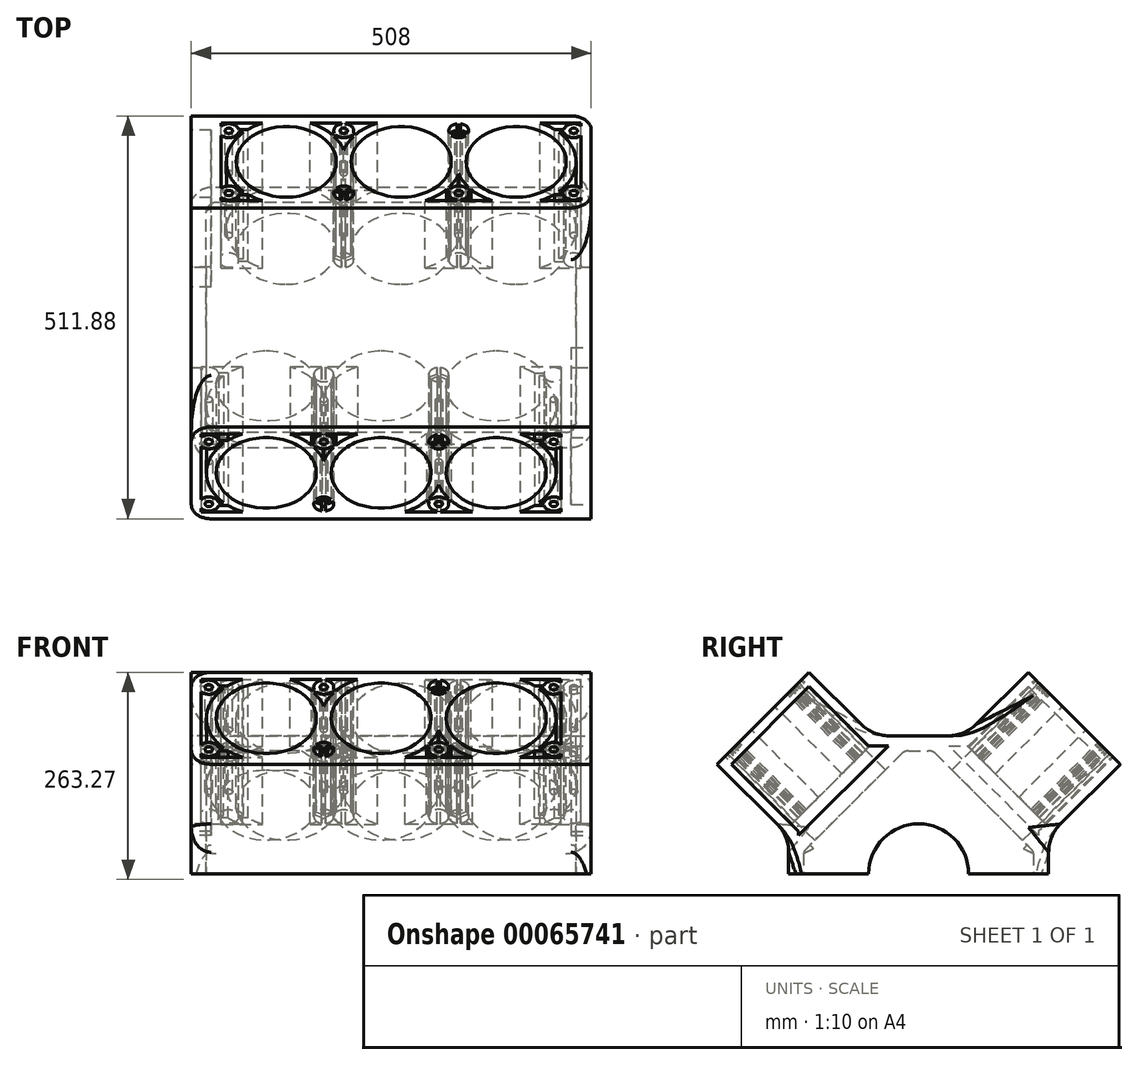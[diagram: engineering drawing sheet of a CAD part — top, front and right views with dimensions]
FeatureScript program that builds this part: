
annotation { "Feature Type Name" : "Feature", "Feature Type Description" : "" }
export const myFeature = defineFeature(function(context is Context, id is Id, definition is map)
    precondition{}
    {
        {
            var Q0;
            Q0=qCreatedBy(makeId("Right.planeOp"),FACE);
            var sketch = newSketch(context, id + "F0", { "sketchPlane" : qUnion([Q0])});
            skLineSegment(sketch, "E0", {"start": v(0, 175.36) * mm, "end": v(0, 0) * mm, "construction": true});
            skLineSegment(sketch, "E1", {"start": v(0, 0) * mm, "end": v(197.57, 197.57) * mm, "construction": true});
            skLineSegment(sketch, "E2", {"start": v(0, 175.36) * mm, "end": v(58.61, 175.36) * mm});
            skLineSegment(sketch, "E3", {"start": v(58.61, 175.36) * mm, "end": v(139.2, 255.94) * mm});
            skLineSegment(sketch, "E4", {"start": v(139.2, 255.94) * mm, "end": v(255.94, 139.2) * mm});
            skLineSegment(sketch, "E5", {"start": v(255.94, 139.2) * mm, "end": v(165.1, 48.36) * mm});
            skLineSegment(sketch, "E6", {"start": v(165.1, 48.36) * mm, "end": v(165.1, 0) * mm});
            skLineSegment(sketch, "E7", {"start": v(63.5, 0) * mm, "end": v(165.1, 0) * mm});
            skArc(sketch, "E8", {"start": v(0, 63.5) * mm, "mid": v(44.9, 44.9) * mm, "end": v(63.5, 0) * mm});
            skLineSegment(sketch, "E9", {"start": v(0, 175.36) * mm, "end": v(0, 63.5) * mm});
            skSolve(sketch);
        }
        {
            var Q0;
            Q0 = qSketchRegion(id + "F0", true);
            extrude(context, id + "F1", {"entities" : qUnion([Q0]), "endBound" : BoundingType.SYMMETRIC, "depth" : 482.6 * mm});
        }
        {
            var Q0;
            Q0=makeQuery(id+"F1.opExtrude","SWEPT_FACE",FACE,{"disambiguationData":[OSD([sQuery(id+"F0.wireOp",EDGE,"E4")])]});
            var sketch = newSketch(context, id + "F2", { "sketchPlane" : qUnion([Q0])});
            skLineSegment(sketch, "E10", {"start": v(146.05, 0) * mm, "end": v(-146.05, 0) * mm, "construction": true});
            skCircle(sketch, "E11", {"center": v(146.05, 0) * mm, "radius": 63.5 * mm});
            skCircle(sketch, "E12", {"center": v(0, 0) * mm, "radius": 63.5 * mm});
            skCircle(sketch, "E13", {"center": v(-146.05, 0) * mm, "radius": 63.5 * mm});
            skSolve(sketch);
        }
        {
            var Q0;
            Q0 = qSketchRegion(id + "F2", true);
            extrude(context, id + "F3", {"entities" : qUnion([Q0]), "operationType" : NewBodyOperationType.REMOVE, "endBound" : BoundingType.THROUGH_ALL, "oppositeDirection" : true, "depth" : 25.4 * mm});
        }
        {
            var Q0;
            Q0=makeQuery(id+"F1.opExtrude","SWEPT_FACE",FACE,{"disambiguationData":[OSD([sQuery(id+"F0.wireOp",EDGE,"E4")])]});
            var sketch = newSketch(context, id + "F4", { "sketchPlane" : qUnion([Q0])});
            skCircle(sketch, "E14", {"center": v(146.05, 0) * mm, "radius": 76 * mm});
            skCircle(sketch, "E15", {"center": v(0, 0) * mm, "radius": 76 * mm});
            skCircle(sketch, "E16", {"center": v(146.05, 0) * mm, "radius": 91.95 * mm, "construction": true});
            skCircle(sketch, "E17", {"center": v(73.03, -55.88) * mm, "radius": 12.7 * mm});
            skLineSegment(sketch, "E18", {"start": v(146.05, 0) * mm, "end": v(146.05, -169.57) * mm, "construction": true});
            skLineSegment(sketch, "E19", {"start": v(146.05, 0) * mm, "end": v(35.62, 0) * mm, "construction": true});
            skCircle(sketch, "E20.MirrorC", {"center": v(219.07, -55.88) * mm, "radius": 12.7 * mm});
            skCircle(sketch, "E21.MirrorC", {"center": v(73.03, 55.88) * mm, "radius": 12.7 * mm});
            skCircle(sketch, "E22.MirrorC", {"center": v(219.07, 55.88) * mm, "radius": 12.7 * mm});
            skLineSegment(sketch, "E23.bottom", {"start": v(228.6, -69.85) * mm, "end": v(-228.6, -69.85) * mm});
            skLineSegment(sketch, "E23.top", {"start": v(228.6, 69.85) * mm, "end": v(-228.6, 69.85) * mm});
            skLineSegment(sketch, "E23.left", {"start": v(228.6, -69.85) * mm, "end": v(228.6, 69.85) * mm});
            skLineSegment(sketch, "E23.right", {"start": v(-228.6, -69.85) * mm, "end": v(-228.6, 69.85) * mm});
            skLineSegment(sketch, "E24", {"start": v(0, -135.82) * mm, "end": v(0, 167.5) * mm, "construction": true});
            skCircle(sketch, "E25.MirrorC", {"center": v(-73.03, -55.88) * mm, "radius": 12.7 * mm});
            skCircle(sketch, "E26.MirrorC", {"center": v(-73.03, 55.88) * mm, "radius": 12.7 * mm});
            skCircle(sketch, "E27.MirrorC", {"center": v(-219.07, 55.88) * mm, "radius": 12.7 * mm});
            skCircle(sketch, "E28.MirrorC", {"center": v(-219.07, -55.88) * mm, "radius": 12.7 * mm});
            skCircle(sketch, "E29.MirrorC", {"center": v(-146.05, 0) * mm, "radius": 76 * mm});
            skSolve(sketch);
        }
        {
            var Q0;
            {var subQ9=sQuery(id+"F4.wireOp",EDGE,"E14");var subQ11=sQuery(id+"F4.wireOp",EDGE,"E23.top");var subQ12=makeQuery(id+"F4.imprint","INTERSECT",VERTEX,{"disambiguationData":[OD(1.0)],"derivedFrom":[subQ9,subQ11]});Q0=makeQuery(id+"F4.imprint","IMPRINT",FACE,{"disambiguationData":[TD([[makeQuery(id+"F4.imprint","IMPRINT",EDGE,{"disambiguationData":[TD([[subQ12,1.0]])],"derivedFrom":subQ9}),-1.0]])]});}
            var Q1;
            Q1=makeQuery(id+"F4.imprint","IMPRINT",FACE,{"disambiguationData":[TD([[makeQuery(id+"F4.imprint","IMPRINT",EDGE,{"derivedFrom":sQuery(id+"F4.wireOp",EDGE,"E17")}),-1.0]])]});
            var Q2;
            Q2=makeQuery(id+"F4.imprint","IMPRINT",FACE,{"disambiguationData":[TD([[makeQuery(id+"F4.imprint","IMPRINT",EDGE,{"derivedFrom":sQuery(id+"F4.wireOp",EDGE,"E21.MirrorC")}),1.0]])]});
            var Q3;
            Q3=makeQuery(id+"F4.imprint","IMPRINT",FACE,{"disambiguationData":[TD([[makeQuery(id+"F4.imprint","IMPRINT",EDGE,{"derivedFrom":sQuery(id+"F4.wireOp",EDGE,"E26.MirrorC")}),-1.0]])]});
            var Q4;
            Q4=makeQuery(id+"F4.imprint","IMPRINT",FACE,{"disambiguationData":[TD([[makeQuery(id+"F4.imprint","IMPRINT",EDGE,{"derivedFrom":sQuery(id+"F4.wireOp",EDGE,"E25.MirrorC")}),1.0]])]});
            var Q5;
            {var subQ0=sQuery(id+"F4.wireOp",EDGE,"E23.right");var subQ1=sQuery(id+"F4.wireOp",EDGE,"E23.bottom");var subQ2=makeQuery(id+"F4.imprint","INTERSECT",VERTEX,{"derivedFrom":[subQ1,subQ0]});Q5=makeQuery(id+"F4.imprint","IMPRINT",FACE,{"disambiguationData":[TD([[makeQuery(id+"F4.imprint","IMPRINT",EDGE,{"disambiguationData":[TD([[subQ2,1.0]])],"derivedFrom":subQ1}),-1.0]])]});}
            extrude(context, id + "F5", {"entities" : qUnion([Q0, Q1, Q2, Q3, Q4, Q5]), "operationType" : NewBodyOperationType.REMOVE, "oppositeDirection" : true, "depth" : 120.65 * mm});
        }
        {
            var Q0;
            {var subQ10=sQuery(id+"F0.wireOp",EDGE,"E4");var subQ11=sQuery(id+"F0.wireOp",EDGE,"E3");Q0=makeQuery(id+"F5.boolean.opBoolean","SPLIT",FACE,{"disambiguationData":[TD([makeQuery(id+"F1.opExtrude","SWEPT_FACE",FACE,{"disambiguationData":[OSD([subQ11])]})])],"derivedFrom":makeQuery(id+"F1.opExtrude","SWEPT_FACE",FACE,{"disambiguationData":[OSD([subQ10])]})});}
            var sketch = newSketch(context, id + "F6", { "sketchPlane" : qUnion([Q0])});
            skLineSegment(sketch, "E30", {"start": v(0, -135.93) * mm, "end": v(0, 142.24) * mm, "construction": true});
            skLineSegment(sketch, "E31", {"start": v(261.24, 0) * mm, "end": v(-274.05, 0) * mm, "construction": true});
            skLineSegment(sketch, "E32", {"start": v(70.53, 57.32) * mm, "end": v(70.53, 70.73) * mm});
            skLineSegment(sketch, "E33", {"start": v(73.03, 55.88) * mm, "end": v(88.64, 46.86) * mm, "construction": true});
            skLineSegment(sketch, "E34", {"start": v(73.03, 46.39) * mm, "end": v(73.03, 55.88) * mm, "construction": true});
            skPoint(sketch, "E35", {"position": v(73.03, 55.88) * mm});
            skLineSegment(sketch, "E36", {"start": v(89.9, 49.03) * mm, "end": v(75.53, 57.32) * mm});
            skLineSegment(sketch, "E37", {"start": v(73.03, 53) * mm, "end": v(59.03, 44.91) * mm});
            skLineSegment(sketch, "E38", {"start": v(73.03, 55.88) * mm, "end": v(57.78, 47.08) * mm, "construction": true});
            skLineSegment(sketch, "E39", {"start": v(75.53, 57.32) * mm, "end": v(75.53, 70.73) * mm});
            skLineSegment(sketch, "E40", {"start": v(56.53, 49.24) * mm, "end": v(70.53, 57.32) * mm});
            skLineSegment(sketch, "E41", {"start": v(87.4, 44.7) * mm, "end": v(73.03, 53) * mm});
            skLineSegment(sketch, "E42", {"start": v(70.53, 70.73) * mm, "end": v(70.53, 57.32) * mm, "construction": true});
            skLineSegment(sketch, "E43", {"start": v(59.03, 44.91) * mm, "end": v(56.53, 49.24) * mm});
            skLineSegment(sketch, "E44", {"start": v(87.4, 44.7) * mm, "end": v(89.9, 49.03) * mm});
            skLineSegment(sketch, "E45", {"start": v(75.53, 70.73) * mm, "end": v(70.53, 70.73) * mm});
            skLineSegment(sketch, "E46", {"start": v(75.53, 70.73) * mm, "end": v(70.53, 70.73) * mm, "construction": true});
            skLineSegment(sketch, "E47.MirrorCS", {"start": v(89.9, -49.03) * mm, "end": v(75.53, -57.32) * mm});
            skLineSegment(sketch, "E48.MirrorCS", {"start": v(87.4, -44.7) * mm, "end": v(73.03, -53) * mm});
            skLineSegment(sketch, "E49.MirrorCS", {"start": v(73.03, -53) * mm, "end": v(59.03, -44.91) * mm});
            skLineSegment(sketch, "E50.MirrorCS", {"start": v(59.03, -44.91) * mm, "end": v(56.53, -49.24) * mm});
            skLineSegment(sketch, "E51.MirrorCS", {"start": v(56.53, -49.24) * mm, "end": v(70.53, -57.32) * mm});
            skLineSegment(sketch, "E52.MirrorCS", {"start": v(70.53, -57.32) * mm, "end": v(70.53, -70.73) * mm});
            skLineSegment(sketch, "E53.MirrorCS", {"start": v(75.53, -70.73) * mm, "end": v(70.53, -70.73) * mm});
            skLineSegment(sketch, "E54.MirrorCS", {"start": v(75.53, -57.32) * mm, "end": v(75.53, -70.73) * mm});
            skLineSegment(sketch, "E55.MirrorCS", {"start": v(87.4, -44.7) * mm, "end": v(89.9, -49.03) * mm});
            skLineSegment(sketch, "E56.MirrorCS", {"start": v(-87.4, 44.7) * mm, "end": v(-89.9, 49.03) * mm});
            skLineSegment(sketch, "E57.MirrorCS", {"start": v(-87.4, 44.7) * mm, "end": v(-73.03, 53) * mm});
            skLineSegment(sketch, "E58.MirrorCS", {"start": v(-73.03, 53) * mm, "end": v(-59.03, 44.91) * mm});
            skLineSegment(sketch, "E59.MirrorCS", {"start": v(-59.03, 44.91) * mm, "end": v(-56.53, 49.24) * mm});
            skLineSegment(sketch, "E60.MirrorCS", {"start": v(-56.53, 49.24) * mm, "end": v(-70.53, 57.32) * mm});
            skLineSegment(sketch, "E61.MirrorCS", {"start": v(-70.53, 57.32) * mm, "end": v(-70.53, 70.73) * mm});
            skLineSegment(sketch, "E62.MirrorCS", {"start": v(-75.53, 70.73) * mm, "end": v(-70.53, 70.73) * mm});
            skLineSegment(sketch, "E63.MirrorCS", {"start": v(-75.53, 57.32) * mm, "end": v(-75.53, 70.73) * mm});
            skLineSegment(sketch, "E64.MirrorCS", {"start": v(-89.9, 49.03) * mm, "end": v(-75.53, 57.32) * mm});
            skLineSegment(sketch, "E65.MirrorCS", {"start": v(-59.03, -44.91) * mm, "end": v(-56.53, -49.24) * mm});
            skLineSegment(sketch, "E66.MirrorCS", {"start": v(-73.03, -53) * mm, "end": v(-59.03, -44.91) * mm});
            skLineSegment(sketch, "E67.MirrorCS", {"start": v(-87.4, -44.7) * mm, "end": v(-73.03, -53) * mm});
            skLineSegment(sketch, "E68.MirrorCS", {"start": v(-87.4, -44.7) * mm, "end": v(-89.9, -49.03) * mm});
            skLineSegment(sketch, "E69.MirrorCS", {"start": v(-89.9, -49.03) * mm, "end": v(-75.53, -57.32) * mm});
            skLineSegment(sketch, "E70.MirrorCS", {"start": v(-75.53, -57.32) * mm, "end": v(-75.53, -70.73) * mm});
            skLineSegment(sketch, "E71.MirrorCS", {"start": v(-75.53, -70.73) * mm, "end": v(-70.53, -70.73) * mm});
            skLineSegment(sketch, "E72.MirrorCS", {"start": v(-70.53, -57.32) * mm, "end": v(-70.53, -70.73) * mm});
            skLineSegment(sketch, "E73.MirrorCS", {"start": v(-56.53, -49.24) * mm, "end": v(-70.53, -57.32) * mm});
            skLineSegment(sketch, "E74", {"start": v(206.37, -55.88) * mm, "end": v(197.56, -55.88) * mm, "construction": true});
            skLineSegment(sketch, "E75", {"start": v(209.05, -58.38) * mm, "end": v(209.05, -53.38) * mm});
            skLineSegment(sketch, "E76", {"start": v(209.05, -53.38) * mm, "end": v(192.06, -53.38) * mm});
            skLineSegment(sketch, "E77", {"start": v(192.06, -53.38) * mm, "end": v(192.06, -58.38) * mm});
            skLineSegment(sketch, "E78", {"start": v(192.06, -58.38) * mm, "end": v(209.05, -58.38) * mm});
            skLineSegment(sketch, "E79.MirrorCS", {"start": v(-209.05, -58.38) * mm, "end": v(-209.05, -53.38) * mm});
            skLineSegment(sketch, "E80.MirrorCS", {"start": v(-192.06, -58.38) * mm, "end": v(-209.05, -58.38) * mm});
            skLineSegment(sketch, "E81.MirrorCS", {"start": v(-192.06, -53.38) * mm, "end": v(-192.06, -58.38) * mm});
            skLineSegment(sketch, "E82.MirrorCS", {"start": v(-209.05, -53.38) * mm, "end": v(-192.06, -53.38) * mm});
            skLineSegment(sketch, "E83.MirrorCS", {"start": v(209.05, 58.38) * mm, "end": v(209.05, 53.38) * mm});
            skLineSegment(sketch, "E84.MirrorCS", {"start": v(192.06, 58.38) * mm, "end": v(209.05, 58.38) * mm});
            skLineSegment(sketch, "E85.MirrorCS", {"start": v(209.05, 53.38) * mm, "end": v(192.06, 53.38) * mm});
            skLineSegment(sketch, "E86.MirrorCS", {"start": v(192.06, 53.38) * mm, "end": v(192.06, 58.38) * mm});
            skLineSegment(sketch, "E87.MirrorCS", {"start": v(-209.05, 53.38) * mm, "end": v(-192.06, 53.38) * mm});
            skLineSegment(sketch, "E88.MirrorCS", {"start": v(-192.06, 53.38) * mm, "end": v(-192.06, 58.38) * mm});
            skLineSegment(sketch, "E89.MirrorCS", {"start": v(-192.06, 58.38) * mm, "end": v(-209.05, 58.38) * mm});
            skLineSegment(sketch, "E90.MirrorCS", {"start": v(-209.05, 58.38) * mm, "end": v(-209.05, 53.38) * mm});
            skSolve(sketch);
        }
        {
            var Q0;
            Q0 = qSketchRegion(id + "F6", true);
            extrude(context, id + "F7", {"entities" : qUnion([Q0]), "operationType" : NewBodyOperationType.ADD, "oppositeDirection" : true, "depth" : 120.65 * mm});
        }
        {
            var Q0;
            {var subQ26=sQuery(id+"F0.wireOp",EDGE,"E3");var subQ32=sQuery(id+"F0.wireOp",EDGE,"E4");Q0=makeQuery(id+"F5.boolean.opBoolean","SPLIT",FACE,{"disambiguationData":[TD([makeQuery(id+"F1.opExtrude","SWEPT_FACE",FACE,{"disambiguationData":[OSD([subQ26])]})])],"derivedFrom":makeQuery(id+"F1.opExtrude","SWEPT_FACE",FACE,{"disambiguationData":[OSD([subQ32])]})});}
            var sketch = newSketch(context, id + "F8", { "sketchPlane" : qUnion([Q0])});
            skCircle(sketch, "E91", {"center": v(219.07, 55.88) * mm, "radius": 4.76 * mm});
            skCircle(sketch, "E92", {"center": v(73.03, 55.88) * mm, "radius": 4.76 * mm});
            skLineSegment(sketch, "E93", {"start": v(0, -161.36) * mm, "end": v(0, 186.57) * mm, "construction": true});
            skLineSegment(sketch, "E94", {"start": v(291.36, 0) * mm, "end": v(-286.68, 0) * mm, "construction": true});
            skCircle(sketch, "E95.MirrorC", {"center": v(219.07, -55.88) * mm, "radius": 4.76 * mm});
            skCircle(sketch, "E96.MirrorC", {"center": v(73.03, -55.88) * mm, "radius": 4.76 * mm});
            skCircle(sketch, "E97.MirrorC", {"center": v(-73.03, -55.88) * mm, "radius": 4.76 * mm});
            skCircle(sketch, "E98.MirrorC", {"center": v(-73.03, 55.88) * mm, "radius": 4.76 * mm});
            skCircle(sketch, "E99.MirrorC", {"center": v(-219.07, -55.88) * mm, "radius": 4.76 * mm});
            skCircle(sketch, "E100.MirrorC", {"center": v(-219.07, 55.88) * mm, "radius": 4.76 * mm});
            skSolve(sketch);
        }
        {
            var Q0;
            Q0 = qSketchRegion(id + "F8", true);
            extrude(context, id + "F9", {"entities" : qUnion([Q0]), "operationType" : NewBodyOperationType.REMOVE, "oppositeDirection" : true, "depth" : 76 * mm});
        }
        {
            var Q0;
            Q0=qCreatedBy(makeId("Front.planeOp"),FACE);
            var sketch = newSketch(context, id + "F10", { "sketchPlane" : qUnion([Q0])});
            skLineSegment(sketch, "E101", {"start": v(-12.7, 175.36) * mm, "end": v(-12.7, 131) * mm, "construction": true});
            skSolve(sketch);
        }
        {
            var Q0;
            Q0=makeQuery(id+"F1.opExtrude","SWEPT_BODY",BODY,{"disambiguationData":[OSD([sQuery(id+"F0.wireOp",EDGE,"E2"),sQuery(id+"F0.wireOp",EDGE,"E3"),sQuery(id+"F0.wireOp",EDGE,"E4"),sQuery(id+"F0.wireOp",EDGE,"E5"),sQuery(id+"F0.wireOp",EDGE,"E6"),sQuery(id+"F0.wireOp",EDGE,"E7"),sQuery(id+"F0.wireOp",EDGE,"E8"),sQuery(id+"F0.wireOp",EDGE,"E9")])]});
            var Q1;
            Q1=sQuery(id+"F10.wireOp",EDGE,"E101");
            circularPattern(context, id + "F11", {"entities" : qUnion([Q0]), "axis" : qUnion([Q1]), "angle" : 180 * degree, "instanceCount" : 2});
        }
        {
            var Q0;
            Q0=makeQuery(id+"F11.opPattern","COPY",FACE,{"derivedFrom":makeQuery(id+"F1.opExtrude","CAP_FACE",FACE,{"disambiguationData":[OSD([sQuery(id+"F0.wireOp",EDGE,"E2"),sQuery(id+"F0.wireOp",EDGE,"E3"),sQuery(id+"F0.wireOp",EDGE,"E4"),sQuery(id+"F0.wireOp",EDGE,"E5"),sQuery(id+"F0.wireOp",EDGE,"E6"),sQuery(id+"F0.wireOp",EDGE,"E7"),sQuery(id+"F0.wireOp",EDGE,"E8"),sQuery(id+"F0.wireOp",EDGE,"E9")])],"isStart":true}),"instanceName":"1"});
            var sketch = newSketch(context, id + "F12", { "sketchPlane" : qUnion([Q0])});
            skLineSegment(sketch, "E102.0", {"start": v(-139.2, 255.94) * mm, "end": v(-255.94, 139.2) * mm});
            skLineSegment(sketch, "E103.0", {"start": v(-58.61, 175.36) * mm, "end": v(-139.2, 255.94) * mm});
            skLineSegment(sketch, "E104.0", {"start": v(0, 175.36) * mm, "end": v(-58.61, 175.36) * mm});
            skLineSegment(sketch, "E105.0", {"start": v(-255.94, 139.2) * mm, "end": v(-165.1, 48.36) * mm});
            skLineSegment(sketch, "E106.0", {"start": v(-165.1, 48.36) * mm, "end": v(-165.1, 0) * mm});
            skLineSegment(sketch, "E107.0", {"start": v(-63.5, 0) * mm, "end": v(-165.1, 0) * mm});
            skArc(sketch, "E108.0", {"start": v(0, 63.5) * mm, "mid": v(-44.9, 44.9) * mm, "end": v(-63.5, 0) * mm});
            skLineSegment(sketch, "E109.0", {"start": v(0, 175.36) * mm, "end": v(0, 63.5) * mm});
            skSolve(sketch);
        }
        {
            var Q0;
            Q0 = qSketchRegion(id + "F12", true);
            var Q1;
            Q1=makeQuery(id+"F1.opExtrude","CAP_FACE",FACE,{"disambiguationData":[OSD([sQuery(id+"F0.wireOp",EDGE,"E2"),sQuery(id+"F0.wireOp",EDGE,"E3"),sQuery(id+"F0.wireOp",EDGE,"E4"),sQuery(id+"F0.wireOp",EDGE,"E5"),sQuery(id+"F0.wireOp",EDGE,"E6"),sQuery(id+"F0.wireOp",EDGE,"E7"),sQuery(id+"F0.wireOp",EDGE,"E8"),sQuery(id+"F0.wireOp",EDGE,"E9")])],"isStart":false});
            extrude(context, id + "F13", {"entities" : qUnion([Q0]), "operationType" : NewBodyOperationType.ADD, "endBound" : BoundingType.UP_TO_SURFACE, "endBoundEntityFace" : qUnion([Q1]), "depth" : 25.4 * mm});
        }
        {
            var Q0;
            Q0=makeQuery(id+"F1.opExtrude","CAP_FACE",FACE,{"disambiguationData":[OSD([sQuery(id+"F0.wireOp",EDGE,"E2"),sQuery(id+"F0.wireOp",EDGE,"E3"),sQuery(id+"F0.wireOp",EDGE,"E4"),sQuery(id+"F0.wireOp",EDGE,"E5"),sQuery(id+"F0.wireOp",EDGE,"E6"),sQuery(id+"F0.wireOp",EDGE,"E7"),sQuery(id+"F0.wireOp",EDGE,"E8"),sQuery(id+"F0.wireOp",EDGE,"E9")])],"isStart":true});
            var sketch = newSketch(context, id + "F14", { "sketchPlane" : qUnion([Q0])});
            skLineSegment(sketch, "E110.0", {"start": v(-58.61, 175.36) * mm, "end": v(-139.2, 255.94) * mm});
            skLineSegment(sketch, "E111.0", {"start": v(-139.2, 255.94) * mm, "end": v(-255.94, 139.2) * mm});
            skLineSegment(sketch, "E112.0", {"start": v(-255.94, 139.2) * mm, "end": v(-165.1, 48.36) * mm});
            skLineSegment(sketch, "E113.0", {"start": v(-165.1, 48.36) * mm, "end": v(-165.1, 0) * mm});
            skLineSegment(sketch, "E114.0", {"start": v(-63.5, 0) * mm, "end": v(-165.1, 0) * mm});
            skArc(sketch, "E115.0", {"start": v(0, 63.5) * mm, "mid": v(-44.9, 44.9) * mm, "end": v(-63.5, 0) * mm});
            skLineSegment(sketch, "E116.0", {"start": v(0, 175.36) * mm, "end": v(-58.61, 175.36) * mm});
            skLineSegment(sketch, "E117.0", {"start": v(0, 175.36) * mm, "end": v(0, 63.5) * mm});
            skSolve(sketch);
        }
        {
            var Q0;
            Q0 = qSketchRegion(id + "F14", true);
            var Q1;
            Q1=makeQuery(id+"F11.opPattern","COPY",FACE,{"derivedFrom":makeQuery(id+"F1.opExtrude","CAP_FACE",FACE,{"disambiguationData":[OSD([sQuery(id+"F0.wireOp",EDGE,"E2"),sQuery(id+"F0.wireOp",EDGE,"E3"),sQuery(id+"F0.wireOp",EDGE,"E4"),sQuery(id+"F0.wireOp",EDGE,"E5"),sQuery(id+"F0.wireOp",EDGE,"E6"),sQuery(id+"F0.wireOp",EDGE,"E7"),sQuery(id+"F0.wireOp",EDGE,"E8"),sQuery(id+"F0.wireOp",EDGE,"E9")])],"isStart":false}),"instanceName":"1"});
            extrude(context, id + "F15", {"entities" : qUnion([Q0]), "operationType" : NewBodyOperationType.ADD, "endBound" : BoundingType.UP_TO_SURFACE, "endBoundEntityFace" : qUnion([Q1]), "depth" : 25.4 * mm});
        }
        {
            var Q0;
            Q0=makeQuery(id+"F13.boolean.opBoolean","MERGE",FACE,{"derivedFrom":[makeQuery(id+"F1.opExtrude","CAP_FACE",FACE,{"disambiguationData":[OSD([sQuery(id+"F0.wireOp",EDGE,"E2"),sQuery(id+"F0.wireOp",EDGE,"E3"),sQuery(id+"F0.wireOp",EDGE,"E4"),sQuery(id+"F0.wireOp",EDGE,"E5"),sQuery(id+"F0.wireOp",EDGE,"E6"),sQuery(id+"F0.wireOp",EDGE,"E7"),sQuery(id+"F0.wireOp",EDGE,"E8"),sQuery(id+"F0.wireOp",EDGE,"E9")])],"isStart":false}),makeQuery(id+"F13.opExtrude","CAP_FACE",FACE,{"disambiguationData":[OSD([sQuery(id+"F12.wireOp",EDGE,"E102.0"),sQuery(id+"F12.wireOp",EDGE,"E103.0"),sQuery(id+"F12.wireOp",EDGE,"E104.0"),sQuery(id+"F12.wireOp",EDGE,"E105.0"),sQuery(id+"F12.wireOp",EDGE,"E106.0"),sQuery(id+"F12.wireOp",EDGE,"E107.0"),sQuery(id+"F12.wireOp",EDGE,"E108.0"),sQuery(id+"F12.wireOp",EDGE,"E109.0")])],"isStart":false})]});
            var sketch = newSketch(context, id + "F16", { "sketchPlane" : qUnion([Q0])});
            skLineSegment(sketch, "E118.0", {"start": v(139.2, 237.98) * mm, "end": v(63.87, 162.66) * mm});
            skLineSegment(sketch, "E118.1", {"start": v(-152.4, 53.62) * mm, "end": v(-152.4, 12.7) * mm});
            skLineSegment(sketch, "E118.2", {"start": v(-237.98, 139.2) * mm, "end": v(-152.4, 53.62) * mm});
            skLineSegment(sketch, "E118.3", {"start": v(-139.2, 237.98) * mm, "end": v(-237.98, 139.2) * mm});
            skLineSegment(sketch, "E118.4", {"start": v(-63.87, 162.66) * mm, "end": v(-139.2, 237.98) * mm});
            skLineSegment(sketch, "E118.5", {"start": v(-152.4, 12.7) * mm, "end": v(-75.13, 12.7) * mm});
            skLineSegment(sketch, "E118.6", {"start": v(63.87, 162.66) * mm, "end": v(-63.87, 162.66) * mm});
            skArc(sketch, "E118.7", {"start": v(-75.13, 12.7) * mm, "mid": v(0, 76.2) * mm, "end": v(75.13, 12.7) * mm});
            skLineSegment(sketch, "E118.8", {"start": v(75.13, 12.7) * mm, "end": v(152.4, 12.7) * mm});
            skLineSegment(sketch, "E118.9", {"start": v(152.4, 12.7) * mm, "end": v(152.4, 53.62) * mm});
            skLineSegment(sketch, "E118.10", {"start": v(152.4, 53.62) * mm, "end": v(237.98, 139.2) * mm});
            skLineSegment(sketch, "E118.11", {"start": v(237.98, 139.2) * mm, "end": v(139.2, 237.98) * mm});
            skLineSegment(sketch, "E119", {"start": v(-38.36, 162.66) * mm, "end": v(-152.4, 48.62) * mm});
            skLineSegment(sketch, "E120", {"start": v(-152.4, 53.62) * mm, "end": v(-152.4, 48.62) * mm});
            skSolve(sketch);
        }
        {
            var Q0;
            Q0=makeQuery(id+"F16.imprint","IMPRINT",FACE,{"disambiguationData":[TD([[makeQuery(id+"F16.imprint","IMPRINT",EDGE,{"derivedFrom":sQuery(id+"F16.wireOp",EDGE,"E118.2")}),1.0]])]});
            extrude(context, id + "F17", {"entities" : qUnion([Q0]), "operationType" : NewBodyOperationType.REMOVE, "oppositeDirection" : true, "depth" : 25.4 * mm});
        }
        {
            var Q0;
            Q0=makeQuery(id+"F15.boolean.opBoolean","MERGE",FACE,{"derivedFrom":[makeQuery(id+"F11.opPattern","COPY",FACE,{"derivedFrom":makeQuery(id+"F1.opExtrude","CAP_FACE",FACE,{"disambiguationData":[OSD([sQuery(id+"F0.wireOp",EDGE,"E2"),sQuery(id+"F0.wireOp",EDGE,"E3"),sQuery(id+"F0.wireOp",EDGE,"E4"),sQuery(id+"F0.wireOp",EDGE,"E5"),sQuery(id+"F0.wireOp",EDGE,"E6"),sQuery(id+"F0.wireOp",EDGE,"E7"),sQuery(id+"F0.wireOp",EDGE,"E8"),sQuery(id+"F0.wireOp",EDGE,"E9")])],"isStart":false}),"instanceName":"1"}),makeQuery(id+"F15.opExtrude","CAP_FACE",FACE,{"disambiguationData":[OSD([sQuery(id+"F14.wireOp",EDGE,"E110.0"),sQuery(id+"F14.wireOp",EDGE,"E111.0"),sQuery(id+"F14.wireOp",EDGE,"E112.0"),sQuery(id+"F14.wireOp",EDGE,"E113.0"),sQuery(id+"F14.wireOp",EDGE,"E114.0"),sQuery(id+"F14.wireOp",EDGE,"E115.0"),sQuery(id+"F14.wireOp",EDGE,"E116.0"),sQuery(id+"F14.wireOp",EDGE,"E117.0")])],"isStart":false})]});
            var sketch = newSketch(context, id + "F18", { "sketchPlane" : qUnion([Q0])});
            skLineSegment(sketch, "E121.0", {"start": v(139.2, 237.98) * mm, "end": v(63.87, 162.66) * mm});
            skLineSegment(sketch, "E121.1", {"start": v(-152.4, 53.62) * mm, "end": v(-152.4, 12.7) * mm});
            skLineSegment(sketch, "E121.2", {"start": v(-237.98, 139.2) * mm, "end": v(-152.4, 53.62) * mm});
            skLineSegment(sketch, "E121.3", {"start": v(-139.2, 237.98) * mm, "end": v(-237.98, 139.2) * mm});
            skLineSegment(sketch, "E121.4", {"start": v(-63.87, 162.66) * mm, "end": v(-139.2, 237.98) * mm});
            skLineSegment(sketch, "E121.5", {"start": v(-152.4, 12.7) * mm, "end": v(-75.13, 12.7) * mm});
            skLineSegment(sketch, "E121.6", {"start": v(63.87, 162.66) * mm, "end": v(-63.87, 162.66) * mm});
            skArc(sketch, "E121.7", {"start": v(-75.13, 12.7) * mm, "mid": v(0, 76.2) * mm, "end": v(75.13, 12.7) * mm});
            skLineSegment(sketch, "E121.8", {"start": v(75.13, 12.7) * mm, "end": v(152.4, 12.7) * mm});
            skLineSegment(sketch, "E121.9", {"start": v(152.4, 12.7) * mm, "end": v(152.4, 53.62) * mm});
            skLineSegment(sketch, "E121.10", {"start": v(152.4, 53.62) * mm, "end": v(237.98, 139.2) * mm});
            skLineSegment(sketch, "E121.11", {"start": v(237.98, 139.2) * mm, "end": v(139.2, 237.98) * mm});
            skLineSegment(sketch, "E122", {"start": v(-152.4, 48.62) * mm, "end": v(-38.36, 162.66) * mm});
            skSolve(sketch);
        }
        {
            var Q0;
            {var subQ0=sQuery(id+"F18.wireOp",EDGE,"E121.2");Q0=makeQuery(id+"F18.imprint","IMPRINT",FACE,{"disambiguationData":[TD([[makeQuery(id+"F18.imprint","IMPRINT",EDGE,{"derivedFrom":subQ0}),1.0]])]});}
            extrude(context, id + "F19", {"entities" : qUnion([Q0]), "operationType" : NewBodyOperationType.REMOVE, "oppositeDirection" : true, "depth" : 25.4 * mm});
        }
        {
            var Q0;
            Q0=qCreatedBy(makeId("Right.planeOp"),FACE);
            var sketch = newSketch(context, id + "F20", { "sketchPlane" : qUnion([Q0])});
            skLineSegment(sketch, "E123", {"start": v(0, 156.3) * mm, "end": v(0, -34.1) * mm, "construction": true});
            skLineSegment(sketch, "E124", {"start": v(0, 156.3) * mm, "end": v(-18, 156.3) * mm});
            skLineSegment(sketch, "E125", {"start": v(-18, 156.31) * mm, "end": v(-146.05, 28.26) * mm});
            skLineSegment(sketch, "E126", {"start": v(-146.05, 28.26) * mm, "end": v(-146.05, -34.1) * mm});
            skLineSegment(sketch, "E127", {"start": v(-146.05, -34.1) * mm, "end": v(0, -34.1) * mm});
            skLineSegment(sketch, "E128.MirrorCS", {"start": v(0, 156.3) * mm, "end": v(18, 156.3) * mm});
            skLineSegment(sketch, "E129.MirrorCS", {"start": v(18, 156.31) * mm, "end": v(146.05, 28.26) * mm});
            skLineSegment(sketch, "E130.MirrorCS", {"start": v(146.05, 28.26) * mm, "end": v(146.05, -34.1) * mm});
            skLineSegment(sketch, "E131.MirrorCS", {"start": v(146.05, -34.1) * mm, "end": v(0, -34.1) * mm});
            skSolve(sketch);
        }
        {
            var Q0;
            Q0 = qSketchRegion(id + "F20", true);
            extrude(context, id + "F21", {"entities" : qUnion([Q0]), "operationType" : NewBodyOperationType.REMOVE, "depth" : 222.25 * mm, "hasSecondDirection" : true, "secondDirectionOppositeDirection" : true, "secondDirectionDepth" : 247.65 * mm});
        }
        {
            var Q0;
            Q0=makeQuery(id+"F21.boolean.opBoolean","COPY",EDGE,{"derivedFrom":makeQuery(id+"F21.opExtrude","CAP_EDGE",EDGE,{"disambiguationData":[OSD([sQuery(id+"F20.wireOp",EDGE,"E125")])],"isStart":true})});
            var Q1;
            Q1=makeQuery(id+"F21.boolean.opBoolean","COPY",EDGE,{"derivedFrom":makeQuery(id+"F21.opExtrude","CAP_EDGE",EDGE,{"disambiguationData":[OSD([sQuery(id+"F20.wireOp",EDGE,"E124"),sQuery(id+"F20.wireOp",EDGE,"E128.MirrorCS")])],"isStart":true})});
            var Q2;
            Q2=makeQuery(id+"F21.boolean.opBoolean","COPY",EDGE,{"derivedFrom":makeQuery(id+"F21.opExtrude","CAP_EDGE",EDGE,{"disambiguationData":[OSD([sQuery(id+"F20.wireOp",EDGE,"E129.MirrorCS")])],"isStart":true})});
            var Q3;
            Q3=makeQuery(id+"F21.boolean.opBoolean","COPY",EDGE,{"derivedFrom":makeQuery(id+"F21.opExtrude","SWEPT_EDGE",EDGE,{"disambiguationData":[OSD([sQuery(id+"F20.wireOp",EDGE,"E125"),sQuery(id+"F20.wireOp",EDGE,"E126")])]})});
            var Q4;
            Q4=makeQuery(id+"F21.boolean.opBoolean","COPY",EDGE,{"derivedFrom":makeQuery(id+"F21.opExtrude","CAP_EDGE",EDGE,{"disambiguationData":[OSD([sQuery(id+"F20.wireOp",EDGE,"E125")])],"isStart":false})});
            var Q5;
            Q5=makeQuery(id+"F21.boolean.opBoolean","COPY",EDGE,{"derivedFrom":makeQuery(id+"F21.opExtrude","CAP_EDGE",EDGE,{"disambiguationData":[OSD([sQuery(id+"F20.wireOp",EDGE,"E124"),sQuery(id+"F20.wireOp",EDGE,"E128.MirrorCS")])],"isStart":false})});
            var Q6;
            Q6=makeQuery(id+"F21.boolean.opBoolean","COPY",EDGE,{"derivedFrom":makeQuery(id+"F21.opExtrude","CAP_EDGE",EDGE,{"disambiguationData":[OSD([sQuery(id+"F20.wireOp",EDGE,"E129.MirrorCS")])],"isStart":false})});
            var Q7;
            Q7=makeQuery(id+"F21.boolean.opBoolean","COPY",EDGE,{"derivedFrom":makeQuery(id+"F21.opExtrude","SWEPT_EDGE",EDGE,{"disambiguationData":[OSD([sQuery(id+"F20.wireOp",EDGE,"E129.MirrorCS"),sQuery(id+"F20.wireOp",EDGE,"E130.MirrorCS")])]})});
            fillet(context, id + "F22", {"entities" : qUnion([Q0, Q1, Q2, Q3, Q4, Q5, Q6, Q7]), "radius" : 6.35 * mm, "tangentPropagation" : true, "allowEdgeOverflow" : false});
        }
        {
            var Q0;
            Q0=makeQuery(id+"F21.boolean.opBoolean","COPY",EDGE,{"derivedFrom":makeQuery(id+"F21.opExtrude","SWEPT_EDGE",EDGE,{"disambiguationData":[OSD([sQuery(id+"F20.wireOp",EDGE,"E128.MirrorCS"),sQuery(id+"F20.wireOp",EDGE,"E129.MirrorCS")])]})});
            var Q1;
            Q1=makeQuery(id+"F21.boolean.opBoolean","COPY",EDGE,{"derivedFrom":makeQuery(id+"F21.opExtrude","SWEPT_EDGE",EDGE,{"disambiguationData":[OSD([sQuery(id+"F20.wireOp",EDGE,"E124"),sQuery(id+"F20.wireOp",EDGE,"E125")])]})});
            var Q2;
            Q2=makeQuery(id+"F21.boolean.opBoolean","COPY",EDGE,{"derivedFrom":makeQuery(id+"F21.opExtrude","CAP_EDGE",EDGE,{"disambiguationData":[OSD([sQuery(id+"F20.wireOp",EDGE,"E126")])],"isStart":false})});
            var Q3;
            Q3=makeQuery(id+"F21.boolean.opBoolean","COPY",EDGE,{"derivedFrom":makeQuery(id+"F21.opExtrude","CAP_EDGE",EDGE,{"disambiguationData":[OSD([sQuery(id+"F20.wireOp",EDGE,"E130.MirrorCS")])],"isStart":false})});
            var Q4;
            Q4=makeQuery(id+"F21.boolean.opBoolean","COPY",EDGE,{"derivedFrom":makeQuery(id+"F21.opExtrude","CAP_EDGE",EDGE,{"disambiguationData":[OSD([sQuery(id+"F20.wireOp",EDGE,"E130.MirrorCS")])],"isStart":true})});
            var Q5;
            Q5=makeQuery(id+"F21.boolean.opBoolean","COPY",EDGE,{"derivedFrom":makeQuery(id+"F21.opExtrude","CAP_EDGE",EDGE,{"disambiguationData":[OSD([sQuery(id+"F20.wireOp",EDGE,"E126")])],"isStart":true})});
            fillet(context, id + "F23", {"entities" : qUnion([Q0, Q1, Q2, Q3, Q4, Q5]), "radius" : 12.7 * mm, "tangentPropagation" : true, "allowEdgeOverflow" : false});
        }
        {
            var Q0;
            Q0=makeQuery(id+"F11.opPattern","COPY",EDGE,{"derivedFrom":makeQuery(id+"F1.opExtrude","CAP_EDGE",EDGE,{"disambiguationData":[OSD([sQuery(id+"F0.wireOp",EDGE,"E5")])],"isStart":false}),"instanceName":"1"});
            var Q1;
            Q1=makeQuery(id+"F11.opPattern","COPY",EDGE,{"derivedFrom":makeQuery(id+"F1.opExtrude","CAP_EDGE",EDGE,{"disambiguationData":[OSD([sQuery(id+"F0.wireOp",EDGE,"E6")])],"isStart":false}),"instanceName":"1"});
            var Q2;
            Q2=makeQuery(id+"F11.opPattern","COPY",EDGE,{"derivedFrom":makeQuery(id+"F1.opExtrude","CAP_EDGE",EDGE,{"disambiguationData":[OSD([sQuery(id+"F0.wireOp",EDGE,"E3")])],"isStart":false}),"instanceName":"1"});
            var Q3;
            Q3=makeQuery(id+"F1.opExtrude","CAP_EDGE",EDGE,{"disambiguationData":[OSD([sQuery(id+"F0.wireOp",EDGE,"E6")])],"isStart":false});
            var Q4;
            Q4=makeQuery(id+"F1.opExtrude","CAP_EDGE",EDGE,{"disambiguationData":[OSD([sQuery(id+"F0.wireOp",EDGE,"E5")])],"isStart":false});
            var Q5;
            Q5=makeQuery(id+"F1.opExtrude","CAP_EDGE",EDGE,{"disambiguationData":[OSD([sQuery(id+"F0.wireOp",EDGE,"E3")])],"isStart":false});
            fillet(context, id + "F24", {"entities" : qUnion([Q0, Q1, Q2, Q3, Q4, Q5]), "radius" : 25.4 * mm, "tangentPropagation" : true, "allowEdgeOverflow" : false});
        }
        {
            var Q0;
            Q0=makeQuery(id+"F13.opExtrude","CAP_EDGE",EDGE,{"disambiguationData":[OSD([sQuery(id+"F12.wireOp",EDGE,"E106.0")])],"isStart":false});
            fillet(context, id + "F25", {"entities" : qUnion([Q0]), "radius" : 25.4 * mm, "tangentPropagation" : true, "allowEdgeOverflow" : false});
        }
        {
            var Q0;
            Q0=makeQuery(id+"F15.opExtrude","CAP_EDGE",EDGE,{"disambiguationData":[OSD([sQuery(id+"F14.wireOp",EDGE,"E113.0")])],"isStart":false});
            fillet(context, id + "F26", {"entities" : qUnion([Q0]), "radius" : 25.4 * mm, "tangentPropagation" : true, "allowEdgeOverflow" : false});
        }
        {
            var Q0;
            Q0=makeQuery(id+"F15.boolean.opBoolean","MERGE",EDGE,{"derivedFrom":[makeQuery(id+"F1.opExtrude","SWEPT_EDGE",EDGE,{"disambiguationData":[OSD([sQuery(id+"F0.wireOp",EDGE,"E2"),sQuery(id+"F0.wireOp",EDGE,"E3")])]}),makeQuery(id+"F15.opExtrude","SWEPT_EDGE",EDGE,{"disambiguationData":[OSD([sQuery(id+"F14.wireOp",EDGE,"E110.0"),sQuery(id+"F14.wireOp",EDGE,"E116.0")])]})]});
            var Q1;
            Q1=makeQuery(id+"F13.boolean.opBoolean","MERGE",EDGE,{"derivedFrom":[makeQuery(id+"F11.opPattern","COPY",EDGE,{"derivedFrom":makeQuery(id+"F1.opExtrude","SWEPT_EDGE",EDGE,{"disambiguationData":[OSD([sQuery(id+"F0.wireOp",EDGE,"E2"),sQuery(id+"F0.wireOp",EDGE,"E3")])]}),"instanceName":"1"}),makeQuery(id+"F13.opExtrude","SWEPT_EDGE",EDGE,{"disambiguationData":[OSD([sQuery(id+"F12.wireOp",EDGE,"E103.0"),sQuery(id+"F12.wireOp",EDGE,"E104.0")])]})]});
            fillet(context, id + "F27", {"entities" : qUnion([Q0, Q1]), "radius" : 50.8 * mm, "tangentPropagation" : true, "allowEdgeOverflow" : false});
        }
        {
            var Q0;
            Q0=makeQuery(id+"F13.boolean.opBoolean","MERGE",EDGE,{"derivedFrom":[makeQuery(id+"F11.opPattern","COPY",EDGE,{"derivedFrom":makeQuery(id+"F1.opExtrude","SWEPT_EDGE",EDGE,{"disambiguationData":[OSD([sQuery(id+"F0.wireOp",EDGE,"E5"),sQuery(id+"F0.wireOp",EDGE,"E6")])]}),"instanceName":"1"}),makeQuery(id+"F13.opExtrude","SWEPT_EDGE",EDGE,{"disambiguationData":[OSD([sQuery(id+"F12.wireOp",EDGE,"E105.0"),sQuery(id+"F12.wireOp",EDGE,"E106.0")])]})]});
            var Q1;
            Q1=makeQuery(id+"F15.boolean.opBoolean","MERGE",EDGE,{"derivedFrom":[makeQuery(id+"F1.opExtrude","SWEPT_EDGE",EDGE,{"disambiguationData":[OSD([sQuery(id+"F0.wireOp",EDGE,"E5"),sQuery(id+"F0.wireOp",EDGE,"E6")])]}),makeQuery(id+"F15.opExtrude","SWEPT_EDGE",EDGE,{"disambiguationData":[OSD([sQuery(id+"F14.wireOp",EDGE,"E112.0"),sQuery(id+"F14.wireOp",EDGE,"E113.0")])]})]});
            fillet(context, id + "F28", {"entities" : qUnion([Q0, Q1]), "radius" : 50.8 * mm, "tangentPropagation" : true, "allowEdgeOverflow" : false});
        }
    });
